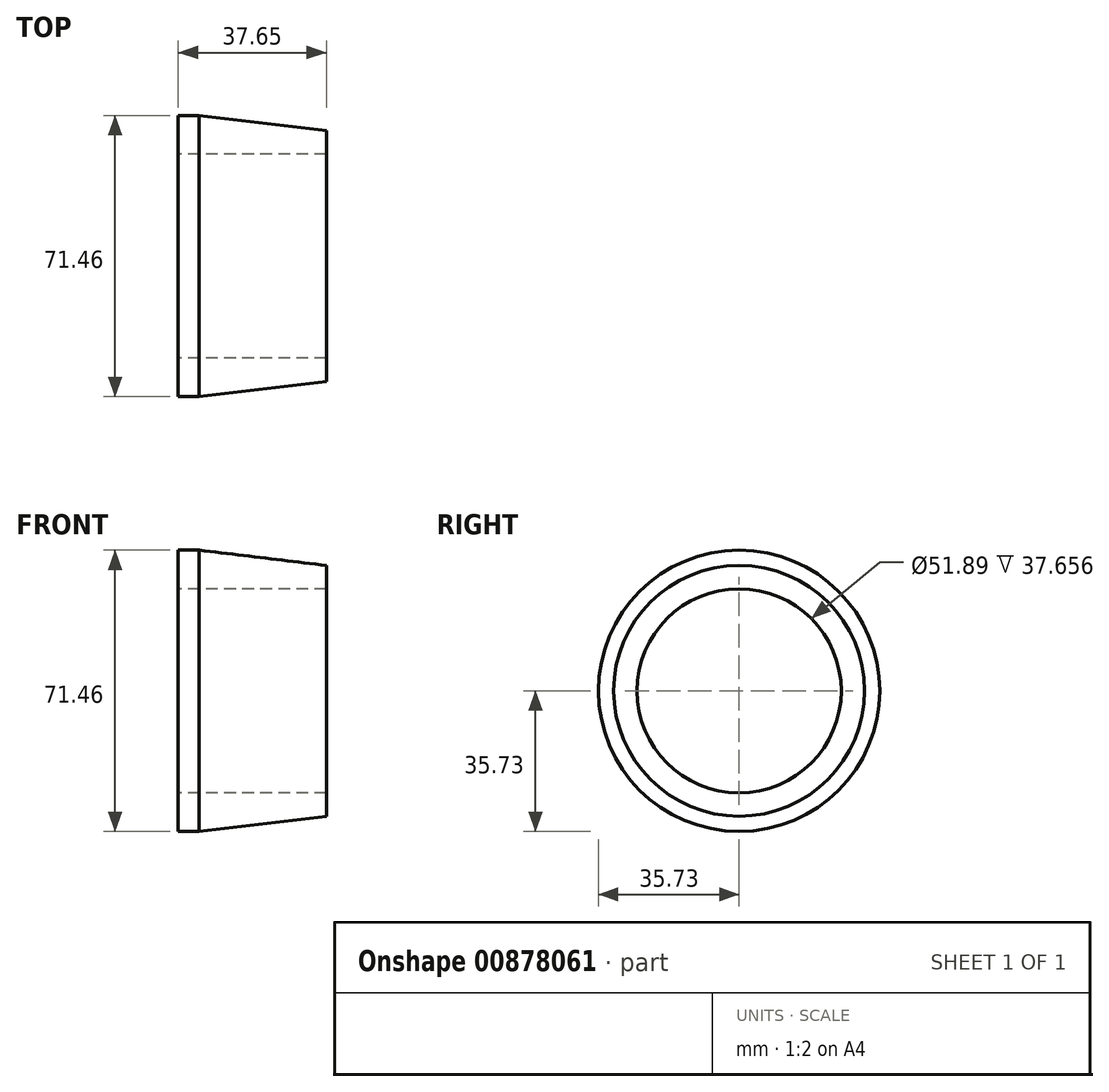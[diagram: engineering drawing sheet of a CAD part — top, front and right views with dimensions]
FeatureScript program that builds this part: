
annotation { "Feature Type Name" : "Feature", "Feature Type Description" : "" }
export const myFeature = defineFeature(function(context is Context, id is Id, definition is map)
    precondition{}
    {
        {
            var Q0;
            Q0=qCreatedBy(makeId("Top.planeOp"),FACE);
            var sketch = newSketch(context, id + "F0", { "sketchPlane" : qUnion([Q0])});
            skLineSegment(sketch, "E0", {"start": v(-44.62, 0) * mm, "end": v(48.77, 0) * mm});
            skSolve(sketch);
        }
        {
            var Q0;
            Q0=qCreatedBy(makeId("Top.planeOp"),FACE);
            var sketch = newSketch(context, id + "F1", { "sketchPlane" : qUnion([Q0])});
            skLineSegment(sketch, "E1", {"start": v(-12.6, 35.73) * mm, "end": v(-12.6, 25.94) * mm});
            skLineSegment(sketch, "E2", {"start": v(-12.6, 25.94) * mm, "end": v(25.05, 25.94) * mm});
            skLineSegment(sketch, "E3", {"start": v(25.05, 25.94) * mm, "end": v(25.05, 31.87) * mm});
            skLineSegment(sketch, "E4", {"start": v(25.05, 31.87) * mm, "end": v(-7.26, 35.73) * mm});
            skLineSegment(sketch, "E5", {"start": v(-7.26, 35.73) * mm, "end": v(-12.6, 35.73) * mm});
            skSolve(sketch);
        }
        {
            var Q0;
            Q0=makeQuery(id+"F1.imprint","IMPRINT",FACE,{"disambiguationData":[TD([[makeQuery(id+"F1.imprint","IMPRINT",EDGE,{"derivedFrom":sQuery(id+"F1.wireOp",EDGE,"E1")}),1.0]])]});
            var Q1;
            Q1=sQuery(id+"F0.wireOp",EDGE,"E0");
            revolve(context, id + "F2", {"surfaceOperationType" : NewSurfaceOperationType.NEW, "entities" : qUnion([Q0]), "axis" : qUnion([Q1]), "revolveType" : RevolveType.FULL});
        }
    });
